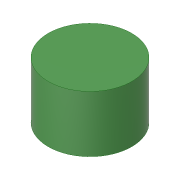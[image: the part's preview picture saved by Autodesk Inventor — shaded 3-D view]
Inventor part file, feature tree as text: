
AUTODESK INVENTOR PART (.ipt)
format: ipt  version: 2017 (Build 210142000, 142)  size: 91,648 bytes
history: native  units: in
note: dims shown in document units (in); Inventor stores cm internally (conversion verified against a paired STEP export)
features: extrude x1, sketch x1
ambient origin geometry x8: Origin, YZ Plane, XZ Plane, XY Plane, X Axis, Y Axis, Z Axis, Center Point
bodies: Solid1 (feature_tree)
feature tree (2):
  extrude  "Extrusion1"  Depth=0.1693in TaperAngle=0.0deg
  sketch  "Sketch1"  dims[d1=0.25in d2=0.1693in d3=0.0in]
